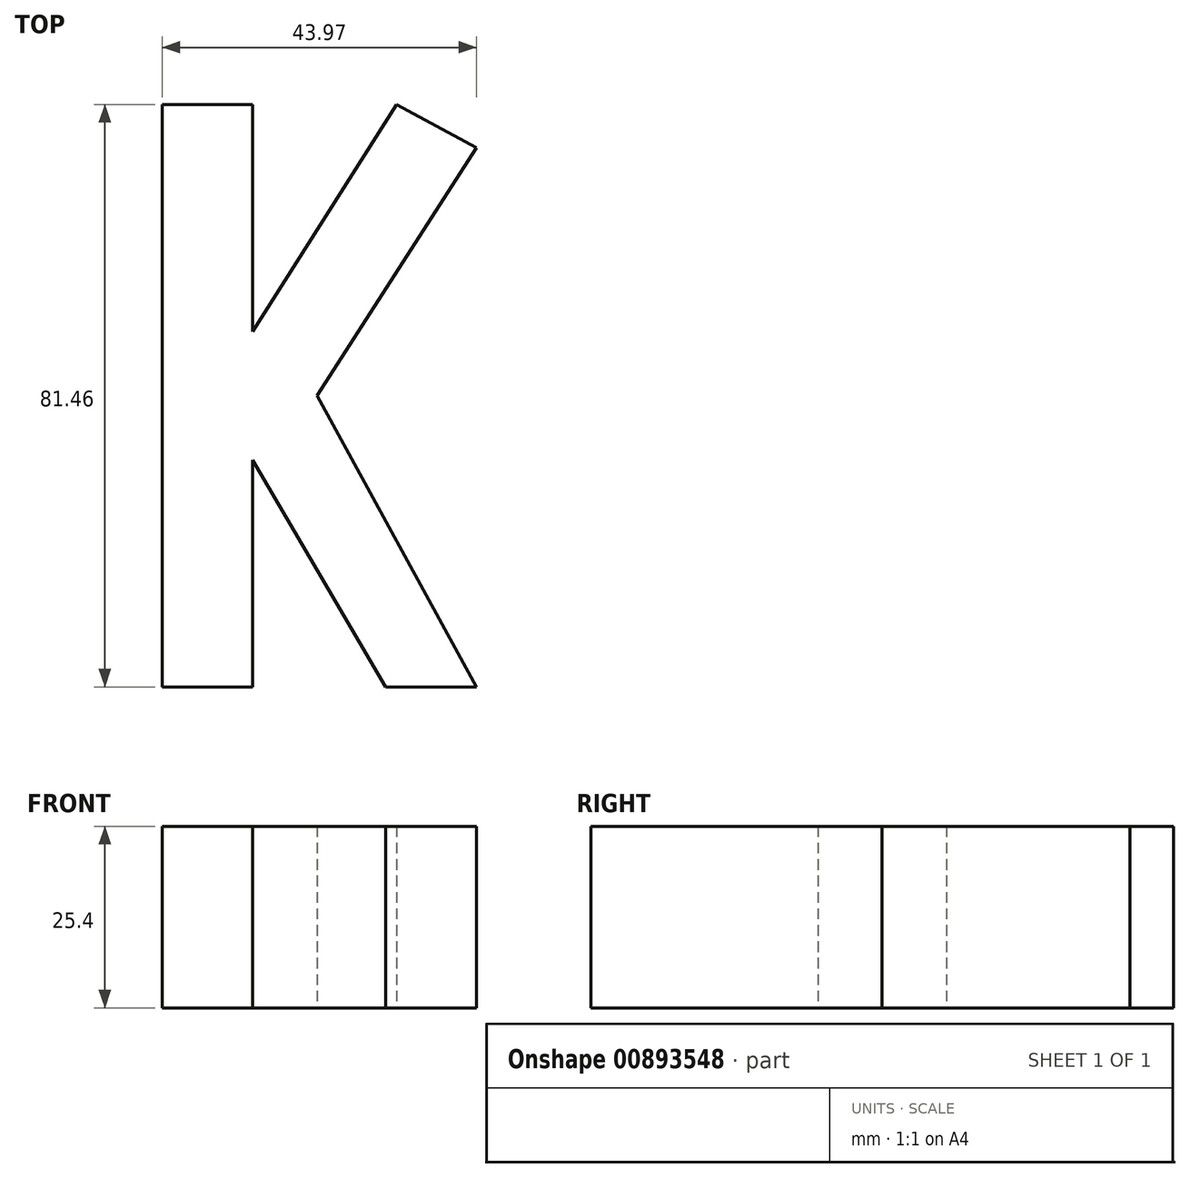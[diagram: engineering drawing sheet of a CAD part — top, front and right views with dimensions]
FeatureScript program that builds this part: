
annotation { "Feature Type Name" : "Feature", "Feature Type Description" : "" }
export const myFeature = defineFeature(function(context is Context, id is Id, definition is map)
    precondition{}
    {
        {
            var Q0;
            Q0=qCreatedBy(makeId("Top.planeOp"),FACE);
            var sketch = newSketch(context, id + "F0", { "sketchPlane" : qUnion([Q0])});
            skLineSegment(sketch, "E0", {"start": v(-43.97, 46.56) * mm, "end": v(-43.97, -34.9) * mm});
            skLineSegment(sketch, "E1", {"start": v(-43.97, -34.9) * mm, "end": v(-31.27, -34.9) * mm});
            skLineSegment(sketch, "E2", {"start": v(-31.27, -34.9) * mm, "end": v(-31.27, -3.15) * mm});
            skLineSegment(sketch, "E3", {"start": v(-31.27, -3.15) * mm, "end": v(-12.7, -34.9) * mm});
            skLineSegment(sketch, "E4", {"start": v(-12.7, -34.9) * mm, "end": v(0, -34.9) * mm});
            skLineSegment(sketch, "E5", {"start": v(0, -34.9) * mm, "end": v(-22.3, 5.83) * mm});
            skLineSegment(sketch, "E6", {"start": v(-22.3, 5.83) * mm, "end": v(0, 40.5) * mm});
            skLineSegment(sketch, "E7", {"start": v(0, 40.5) * mm, "end": v(-11.16, 46.56) * mm});
            skLineSegment(sketch, "E8", {"start": v(-11.16, 46.56) * mm, "end": v(-31.27, 14.8) * mm});
            skLineSegment(sketch, "E9", {"start": v(-31.27, 14.8) * mm, "end": v(-31.27, 46.56) * mm});
            skLineSegment(sketch, "E10", {"start": v(-31.27, 46.56) * mm, "end": v(-43.97, 46.56) * mm});
            skLineSegment(sketch, "E11", {"start": v(-31.27, -3.15) * mm, "end": v(-22.3, 5.83) * mm});
            skLineSegment(sketch, "E12", {"start": v(-22.3, 5.83) * mm, "end": v(-31.27, 14.8) * mm});
            skSolve(sketch);
        }
        {
            var Q0;
            Q0=makeQuery(id+"F0.imprint","IMPRINT",FACE,{"disambiguationData":[TD([[makeQuery(id+"F0.imprint","IMPRINT",EDGE,{"derivedFrom":sQuery(id+"F0.wireOp",EDGE,"E0")}),1.0]])]});
            var Q1;
            Q1=makeQuery(id+"F0.imprint","IMPRINT",FACE,{"disambiguationData":[TD([[makeQuery(id+"F0.imprint","IMPRINT",EDGE,{"derivedFrom":sQuery(id+"F0.wireOp",EDGE,"E6")}),1.0]])]});
            var Q2;
            Q2=makeQuery(id+"F0.imprint","IMPRINT",FACE,{"disambiguationData":[TD([[makeQuery(id+"F0.imprint","IMPRINT",EDGE,{"derivedFrom":sQuery(id+"F0.wireOp",EDGE,"E3")}),1.0]])]});
            extrude(context, id + "F1", {"entities" : qUnion([Q0, Q1, Q2]), "depth" : 25.4 * mm, "offsetDistance" : 25.4 * mm});
        }
    });
